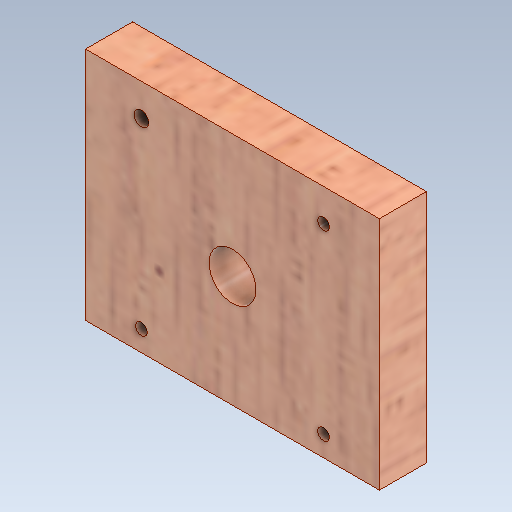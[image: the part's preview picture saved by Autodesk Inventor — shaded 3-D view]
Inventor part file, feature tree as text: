
AUTODESK INVENTOR PART (.ipt)
format: ipt  version: 2020 (Build 240168000, 168)  size: 249,856 bytes
history: native  units: mm
features: reference x4, other x3, extrude x2, sketch x2
ambient origin geometry x8: Origin, YZ Plane, XZ Plane, XY Plane, X Axis, Y Axis, Z Axis, Center Point
bodies: Solid1 (feature_tree)
feature tree (11):
  extrude  "Extrusion1"  Depth=40.0mm
  extrude  "Extrusion5"  Depth=8.0mm
  sketch  "Sketch1"  dims[d0=50.0mm d1=40.0mm]
  sketch  "Sketch5"  dims[d2=8.0mm d3=0.0mm d29=8.0mm d30=0.0mm d31=0.0mm]
  reference  "Reference1"
  reference  "Reference2"
  reference  "Reference3"
  reference  "Reference4"
  parser-record x1  (decoder bookkeeping rows leaked as tree rows — omitted from the tree; the rows remain in map.json)
  other  "0005-00-00 Ansamblu_General.iam"
  other  "0005-10-1001 NEMA17 - Motor de passo:4"
note: 1 file-system path scrubbed to <path> (originals preserved in map.json)
